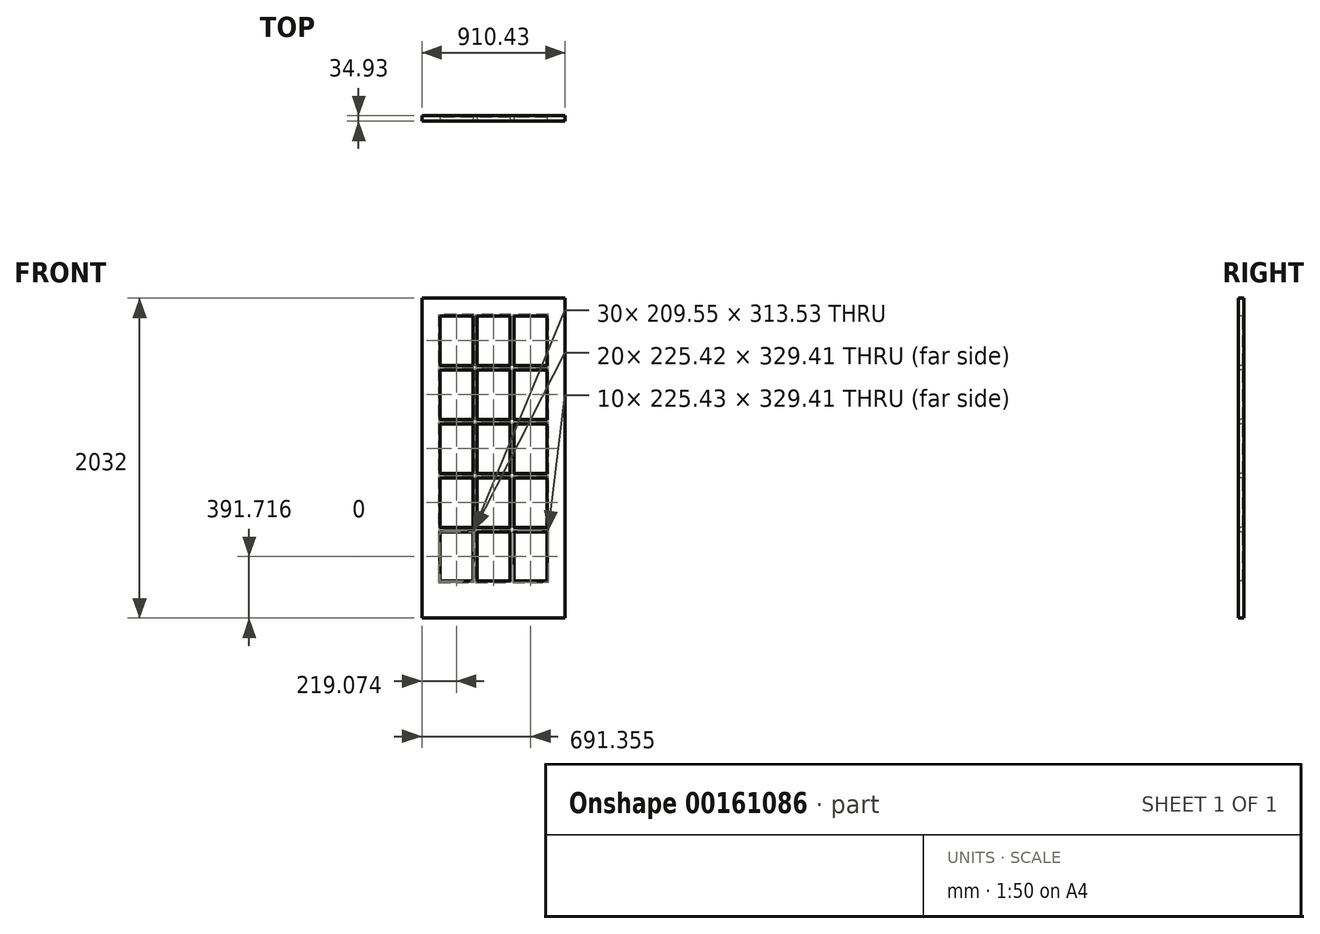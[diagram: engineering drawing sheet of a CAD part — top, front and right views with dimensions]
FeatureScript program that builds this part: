
annotation { "Feature Type Name" : "Feature", "Feature Type Description" : "" }
export const myFeature = defineFeature(function(context is Context, id is Id, definition is map)
    precondition{}
    {
        {
            var Q0;
            Q0=qCreatedBy(makeId("Top.planeOp"),FACE);
            var sketch = newSketch(context, id + "F0", { "sketchPlane" : qUnion([Q0])});
            skLineSegment(sketch, "E0.bottom", {"start": v(0, 0) * mm, "end": v(-910.43, 0) * mm});
            skLineSegment(sketch, "E0.top", {"start": v(0, 34.93) * mm, "end": v(-910.43, 34.93) * mm});
            skLineSegment(sketch, "E0.left", {"start": v(0, 0) * mm, "end": v(0, 34.93) * mm});
            skLineSegment(sketch, "E0.right", {"start": v(-910.43, 0) * mm, "end": v(-910.43, 34.93) * mm});
            skSolve(sketch);
        }
        {
            var Q0;
            Q0=qSketchRegion(id+"F0",true);
            extrude(context, id + "F1", {"entities" : qUnion([Q0]), "depth" : 2032 * mm});
        }
        {
            var Q0;
            Q0=qCreatedBy(makeId("Front.planeOp"),FACE);
            var sketch = newSketch(context, id + "F2", { "sketchPlane" : qUnion([Q0])});
            skPoint(sketch, "E1.0", {"position": v(-910.43, 2032) * mm});
            skPoint(sketch, "E2.0", {"position": v(0, 2032) * mm});
            skPoint(sketch, "E3.0", {"position": v(-910.43, 0) * mm});
            skPoint(sketch, "E4.0", {"position": v(0, 0) * mm});
            skPoint(sketch, "E5.0", {"position": v(-910.43, 1016) * mm});
            skPoint(sketch, "E6.0", {"position": v(-455.22, 2032) * mm});
            skPoint(sketch, "E7.0", {"position": v(0, 1016) * mm});
            skPoint(sketch, "E8.0", {"position": v(-455.22, 0) * mm});
            skLineSegment(sketch, "E9", {"start": v(-910.43, -186.31) * mm, "end": v(-804.07, -186.31) * mm, "construction": true});
            skLineSegment(sketch, "E10", {"start": v(-804.07, -186.31) * mm, "end": v(-796.13, -186.31) * mm, "construction": true});
            skLineSegment(sketch, "E11", {"start": v(-796.13, -186.31) * mm, "end": v(-586.58, -186.31) * mm, "construction": true});
            skLineSegment(sketch, "E12", {"start": v(-586.58, -186.31) * mm, "end": v(-560, -186.31) * mm, "construction": true});
            skLineSegment(sketch, "E13", {"start": v(-560, -186.31) * mm, "end": v(-350.44, -186.31) * mm, "construction": true});
            skLineSegment(sketch, "E14", {"start": v(-350.44, -186.31) * mm, "end": v(-323.85, -186.31) * mm, "construction": true});
            skLineSegment(sketch, "E15", {"start": v(-323.85, -186.31) * mm, "end": v(-114.3, -186.31) * mm, "construction": true});
            skLineSegment(sketch, "E16", {"start": v(-114.3, -186.31) * mm, "end": v(-106.36, -186.31) * mm, "construction": true});
            skLineSegment(sketch, "E17", {"start": v(-106.36, -186.31) * mm, "end": v(0, -186.31) * mm, "construction": true});
            skLineSegment(sketch, "E18", {"start": v(-1196.98, 2032) * mm, "end": v(-1196.98, 1927.22) * mm, "construction": true});
            skLineSegment(sketch, "E19", {"start": v(-1196.98, 1927.22) * mm, "end": v(-1196.98, 1919.29) * mm, "construction": true});
            skLineSegment(sketch, "E20", {"start": v(-1196.98, 1919.29) * mm, "end": v(-1196.98, 1605.76) * mm, "construction": true});
            skLineSegment(sketch, "E21", {"start": v(-1196.98, 1605.76) * mm, "end": v(-1196.98, 1576.59) * mm, "construction": true});
            skLineSegment(sketch, "E22", {"start": v(-1196.98, 1576.59) * mm, "end": v(-1196.98, 1263.05) * mm, "construction": true});
            skLineSegment(sketch, "E23", {"start": v(-1196.98, 1263.05) * mm, "end": v(-1196.98, 1233.88) * mm, "construction": true});
            skLineSegment(sketch, "E24", {"start": v(-1196.98, 1233.88) * mm, "end": v(-1196.98, 920.35) * mm, "construction": true});
            skLineSegment(sketch, "E25", {"start": v(-1196.98, 920.35) * mm, "end": v(-1196.98, 891.18) * mm, "construction": true});
            skLineSegment(sketch, "E26", {"start": v(-1196.98, 577.65) * mm, "end": v(-1196.98, 548.48) * mm, "construction": true});
            skLineSegment(sketch, "E27", {"start": v(-1196.98, 234.95) * mm, "end": v(-1196.98, 227.01) * mm, "construction": true});
            skLineSegment(sketch, "E28", {"start": v(-1196.98, 227.01) * mm, "end": v(-1196.98, 0) * mm, "construction": true});
            skLineSegment(sketch, "E29", {"start": v(-1196.98, 548.48) * mm, "end": v(-1196.98, 234.95) * mm, "construction": true});
            skLineSegment(sketch, "E30", {"start": v(-1196.98, 891.18) * mm, "end": v(-1196.98, 577.65) * mm, "construction": true});
            skLineSegment(sketch, "E31.bottom", {"start": v(-796.13, 234.95) * mm, "end": v(-586.58, 234.95) * mm});
            skLineSegment(sketch, "E31.top", {"start": v(-796.13, 548.48) * mm, "end": v(-586.58, 548.48) * mm});
            skLineSegment(sketch, "E31.left", {"start": v(-796.13, 234.95) * mm, "end": v(-796.13, 548.48) * mm});
            skLineSegment(sketch, "E31.right", {"start": v(-586.58, 234.95) * mm, "end": v(-586.58, 548.48) * mm});
            skLineSegment(sketch, "E32.bottom", {"start": v(-560, 234.95) * mm, "end": v(-350.44, 234.95) * mm});
            skLineSegment(sketch, "E32.top", {"start": v(-560, 548.48) * mm, "end": v(-350.44, 548.48) * mm});
            skLineSegment(sketch, "E32.left", {"start": v(-560, 234.95) * mm, "end": v(-560, 548.48) * mm});
            skLineSegment(sketch, "E32.right", {"start": v(-350.44, 234.95) * mm, "end": v(-350.44, 548.48) * mm});
            skLineSegment(sketch, "E33.bottom", {"start": v(-323.85, 548.48) * mm, "end": v(-114.3, 548.48) * mm});
            skLineSegment(sketch, "E33.top", {"start": v(-323.85, 234.95) * mm, "end": v(-114.3, 234.95) * mm});
            skLineSegment(sketch, "E33.left", {"start": v(-323.85, 548.48) * mm, "end": v(-323.85, 234.95) * mm});
            skLineSegment(sketch, "E33.right", {"start": v(-114.3, 548.48) * mm, "end": v(-114.3, 234.95) * mm});
            skLineSegment(sketch, "E34.bottom", {"start": v(-796.13, 577.65) * mm, "end": v(-586.58, 577.65) * mm});
            skLineSegment(sketch, "E34.top", {"start": v(-796.13, 891.18) * mm, "end": v(-586.58, 891.18) * mm});
            skLineSegment(sketch, "E34.left", {"start": v(-796.13, 577.65) * mm, "end": v(-796.13, 891.18) * mm});
            skLineSegment(sketch, "E34.right", {"start": v(-586.58, 577.65) * mm, "end": v(-586.58, 891.18) * mm});
            skLineSegment(sketch, "E35.bottom", {"start": v(-560, 577.65) * mm, "end": v(-350.44, 577.65) * mm});
            skLineSegment(sketch, "E35.top", {"start": v(-560, 891.18) * mm, "end": v(-350.44, 891.18) * mm});
            skLineSegment(sketch, "E35.left", {"start": v(-560, 577.65) * mm, "end": v(-560, 891.18) * mm});
            skLineSegment(sketch, "E35.right", {"start": v(-350.44, 577.65) * mm, "end": v(-350.44, 891.18) * mm});
            skLineSegment(sketch, "E36.bottom", {"start": v(-323.85, 577.65) * mm, "end": v(-114.3, 577.65) * mm});
            skLineSegment(sketch, "E36.top", {"start": v(-323.85, 891.18) * mm, "end": v(-114.3, 891.18) * mm});
            skLineSegment(sketch, "E36.left", {"start": v(-323.85, 577.65) * mm, "end": v(-323.85, 891.18) * mm});
            skLineSegment(sketch, "E36.right", {"start": v(-114.3, 577.65) * mm, "end": v(-114.3, 891.18) * mm});
            skLineSegment(sketch, "E37.bottom", {"start": v(-796.13, 920.35) * mm, "end": v(-586.58, 920.35) * mm});
            skLineSegment(sketch, "E37.top", {"start": v(-796.13, 1233.88) * mm, "end": v(-586.58, 1233.88) * mm});
            skLineSegment(sketch, "E37.left", {"start": v(-796.13, 920.35) * mm, "end": v(-796.13, 1233.88) * mm});
            skLineSegment(sketch, "E37.right", {"start": v(-586.58, 920.35) * mm, "end": v(-586.58, 1233.88) * mm});
            skLineSegment(sketch, "E38.bottom", {"start": v(-560, 920.35) * mm, "end": v(-350.44, 920.35) * mm});
            skLineSegment(sketch, "E38.top", {"start": v(-560, 1233.88) * mm, "end": v(-350.44, 1233.88) * mm});
            skLineSegment(sketch, "E38.left", {"start": v(-560, 920.35) * mm, "end": v(-560, 1233.88) * mm});
            skLineSegment(sketch, "E38.right", {"start": v(-350.44, 920.35) * mm, "end": v(-350.44, 1233.88) * mm});
            skLineSegment(sketch, "E39.bottom", {"start": v(-323.85, 920.35) * mm, "end": v(-114.3, 920.35) * mm});
            skLineSegment(sketch, "E39.top", {"start": v(-323.85, 1233.88) * mm, "end": v(-114.3, 1233.88) * mm});
            skLineSegment(sketch, "E39.left", {"start": v(-323.85, 920.35) * mm, "end": v(-323.85, 1233.88) * mm});
            skLineSegment(sketch, "E39.right", {"start": v(-114.3, 920.35) * mm, "end": v(-114.3, 1233.88) * mm});
            skLineSegment(sketch, "E40.bottom", {"start": v(-796.13, 1263.05) * mm, "end": v(-586.58, 1263.05) * mm});
            skLineSegment(sketch, "E40.top", {"start": v(-796.13, 1576.59) * mm, "end": v(-586.58, 1576.59) * mm});
            skLineSegment(sketch, "E40.left", {"start": v(-796.13, 1263.05) * mm, "end": v(-796.13, 1576.59) * mm});
            skLineSegment(sketch, "E40.right", {"start": v(-586.58, 1263.05) * mm, "end": v(-586.58, 1576.59) * mm});
            skLineSegment(sketch, "E41.bottom", {"start": v(-560, 1263.05) * mm, "end": v(-350.44, 1263.05) * mm});
            skLineSegment(sketch, "E41.top", {"start": v(-560, 1576.59) * mm, "end": v(-350.44, 1576.59) * mm});
            skLineSegment(sketch, "E41.left", {"start": v(-560, 1263.05) * mm, "end": v(-560, 1576.59) * mm});
            skLineSegment(sketch, "E41.right", {"start": v(-350.44, 1263.05) * mm, "end": v(-350.44, 1576.59) * mm});
            skLineSegment(sketch, "E42.bottom", {"start": v(-323.85, 1263.05) * mm, "end": v(-114.3, 1263.05) * mm});
            skLineSegment(sketch, "E42.top", {"start": v(-323.85, 1576.59) * mm, "end": v(-114.3, 1576.59) * mm});
            skLineSegment(sketch, "E42.left", {"start": v(-323.85, 1263.05) * mm, "end": v(-323.85, 1576.59) * mm});
            skLineSegment(sketch, "E42.right", {"start": v(-114.3, 1263.05) * mm, "end": v(-114.3, 1576.59) * mm});
            skLineSegment(sketch, "E43.bottom", {"start": v(-796.13, 1605.76) * mm, "end": v(-586.58, 1605.76) * mm});
            skLineSegment(sketch, "E43.top", {"start": v(-796.13, 1919.29) * mm, "end": v(-586.58, 1919.29) * mm});
            skLineSegment(sketch, "E43.left", {"start": v(-796.13, 1605.76) * mm, "end": v(-796.13, 1919.29) * mm});
            skLineSegment(sketch, "E43.right", {"start": v(-586.58, 1605.76) * mm, "end": v(-586.58, 1919.29) * mm});
            skLineSegment(sketch, "E44.bottom", {"start": v(-560, 1605.76) * mm, "end": v(-350.44, 1605.76) * mm});
            skLineSegment(sketch, "E44.top", {"start": v(-560, 1919.29) * mm, "end": v(-350.44, 1919.29) * mm});
            skLineSegment(sketch, "E44.left", {"start": v(-560, 1605.76) * mm, "end": v(-560, 1919.29) * mm});
            skLineSegment(sketch, "E44.right", {"start": v(-350.44, 1605.76) * mm, "end": v(-350.44, 1919.29) * mm});
            skLineSegment(sketch, "E45.bottom", {"start": v(-323.85, 1605.76) * mm, "end": v(-114.3, 1605.76) * mm});
            skLineSegment(sketch, "E45.top", {"start": v(-323.85, 1919.29) * mm, "end": v(-114.3, 1919.29) * mm});
            skLineSegment(sketch, "E45.left", {"start": v(-323.85, 1605.76) * mm, "end": v(-323.85, 1919.29) * mm});
            skLineSegment(sketch, "E45.right", {"start": v(-114.3, 1605.76) * mm, "end": v(-114.3, 1919.29) * mm});
            skSolve(sketch);
        }
        {
            var Q0;
            Q0 = qSketchRegion(id + "F2", true);
            extrude(context, id + "F3", {"entities" : qUnion([Q0]), "operationType" : NewBodyOperationType.REMOVE, "endBound" : BoundingType.THROUGH_ALL, "oppositeDirection" : true, "depth" : 426.72 * mm});
        }
        {
            var Q0;
            Q0=makeQuery(id+"F3.boolean.opBoolean","COPY",EDGE,{"derivedFrom":makeQuery(id+"F3.opExtrude","CAP_EDGE",EDGE,{"disambiguationData":[OSD([sQuery(id+"F2.wireOp",EDGE,"E43.right")])],"isStart":true})});
            var Q1;
            Q1=makeQuery(id+"F3.boolean.opBoolean","COPY",EDGE,{"derivedFrom":makeQuery(id+"F3.opExtrude","CAP_EDGE",EDGE,{"disambiguationData":[OSD([sQuery(id+"F2.wireOp",EDGE,"E43.bottom")])],"isStart":true})});
            var Q2;
            Q2=makeQuery(id+"F3.boolean.opBoolean","COPY",EDGE,{"derivedFrom":makeQuery(id+"F3.opExtrude","CAP_EDGE",EDGE,{"disambiguationData":[OSD([sQuery(id+"F2.wireOp",EDGE,"E44.left")])],"isStart":true})});
            var Q3;
            Q3=makeQuery(id+"F3.boolean.opBoolean","COPY",EDGE,{"derivedFrom":makeQuery(id+"F3.opExtrude","CAP_EDGE",EDGE,{"disambiguationData":[OSD([sQuery(id+"F2.wireOp",EDGE,"E44.bottom")])],"isStart":true})});
            var Q4;
            Q4=makeQuery(id+"F3.boolean.opBoolean","COPY",EDGE,{"derivedFrom":makeQuery(id+"F3.opExtrude","CAP_EDGE",EDGE,{"disambiguationData":[OSD([sQuery(id+"F2.wireOp",EDGE,"E41.left")])],"isStart":true})});
            var Q5;
            Q5=makeQuery(id+"F3.boolean.opBoolean","COPY",EDGE,{"derivedFrom":makeQuery(id+"F3.opExtrude","CAP_EDGE",EDGE,{"disambiguationData":[OSD([sQuery(id+"F2.wireOp",EDGE,"E40.top")])],"isStart":true})});
            var Q6;
            Q6=makeQuery(id+"F3.boolean.opBoolean","COPY",EDGE,{"derivedFrom":makeQuery(id+"F3.opExtrude","CAP_EDGE",EDGE,{"disambiguationData":[OSD([sQuery(id+"F2.wireOp",EDGE,"E40.right")])],"isStart":true})});
            var Q7;
            Q7=makeQuery(id+"F3.boolean.opBoolean","COPY",EDGE,{"derivedFrom":makeQuery(id+"F3.opExtrude","CAP_EDGE",EDGE,{"disambiguationData":[OSD([sQuery(id+"F2.wireOp",EDGE,"E44.right")])],"isStart":true})});
            var Q8;
            Q8=makeQuery(id+"F3.boolean.opBoolean","COPY",EDGE,{"derivedFrom":makeQuery(id+"F3.opExtrude","CAP_EDGE",EDGE,{"disambiguationData":[OSD([sQuery(id+"F2.wireOp",EDGE,"E41.top")])],"isStart":true})});
            var Q9;
            Q9=makeQuery(id+"F3.boolean.opBoolean","COPY",EDGE,{"derivedFrom":makeQuery(id+"F3.opExtrude","CAP_EDGE",EDGE,{"disambiguationData":[OSD([sQuery(id+"F2.wireOp",EDGE,"E41.right")])],"isStart":true})});
            var Q10;
            Q10=makeQuery(id+"F3.boolean.opBoolean","COPY",EDGE,{"derivedFrom":makeQuery(id+"F3.opExtrude","CAP_EDGE",EDGE,{"disambiguationData":[OSD([sQuery(id+"F2.wireOp",EDGE,"E42.left")])],"isStart":true})});
            var Q11;
            Q11=makeQuery(id+"F3.boolean.opBoolean","COPY",EDGE,{"derivedFrom":makeQuery(id+"F3.opExtrude","CAP_EDGE",EDGE,{"disambiguationData":[OSD([sQuery(id+"F2.wireOp",EDGE,"E42.top")])],"isStart":true})});
            var Q12;
            Q12=makeQuery(id+"F3.boolean.opBoolean","COPY",EDGE,{"derivedFrom":makeQuery(id+"F3.opExtrude","CAP_EDGE",EDGE,{"disambiguationData":[OSD([sQuery(id+"F2.wireOp",EDGE,"E45.bottom")])],"isStart":true})});
            var Q13;
            Q13=makeQuery(id+"F3.boolean.opBoolean","COPY",EDGE,{"derivedFrom":makeQuery(id+"F3.opExtrude","CAP_EDGE",EDGE,{"disambiguationData":[OSD([sQuery(id+"F2.wireOp",EDGE,"E45.left")])],"isStart":true})});
            var Q14;
            Q14=makeQuery(id+"F3.boolean.opBoolean","COPY",EDGE,{"derivedFrom":makeQuery(id+"F3.opExtrude","CAP_EDGE",EDGE,{"disambiguationData":[OSD([sQuery(id+"F2.wireOp",EDGE,"E40.bottom")])],"isStart":true})});
            var Q15;
            Q15=makeQuery(id+"F3.boolean.opBoolean","COPY",EDGE,{"derivedFrom":makeQuery(id+"F3.opExtrude","CAP_EDGE",EDGE,{"disambiguationData":[OSD([sQuery(id+"F2.wireOp",EDGE,"E37.top")])],"isStart":true})});
            var Q16;
            Q16=makeQuery(id+"F3.boolean.opBoolean","COPY",EDGE,{"derivedFrom":makeQuery(id+"F3.opExtrude","CAP_EDGE",EDGE,{"disambiguationData":[OSD([sQuery(id+"F2.wireOp",EDGE,"E37.bottom")])],"isStart":true})});
            var Q17;
            Q17=makeQuery(id+"F3.boolean.opBoolean","COPY",EDGE,{"derivedFrom":makeQuery(id+"F3.opExtrude","CAP_EDGE",EDGE,{"disambiguationData":[OSD([sQuery(id+"F2.wireOp",EDGE,"E34.top")])],"isStart":true})});
            var Q18;
            Q18=makeQuery(id+"F3.boolean.opBoolean","COPY",EDGE,{"derivedFrom":makeQuery(id+"F3.opExtrude","CAP_EDGE",EDGE,{"disambiguationData":[OSD([sQuery(id+"F2.wireOp",EDGE,"E34.bottom")])],"isStart":true})});
            var Q19;
            Q19=makeQuery(id+"F3.boolean.opBoolean","COPY",EDGE,{"derivedFrom":makeQuery(id+"F3.opExtrude","CAP_EDGE",EDGE,{"disambiguationData":[OSD([sQuery(id+"F2.wireOp",EDGE,"E31.top")])],"isStart":true})});
            var Q20;
            Q20=makeQuery(id+"F3.boolean.opBoolean","COPY",EDGE,{"derivedFrom":makeQuery(id+"F3.opExtrude","CAP_EDGE",EDGE,{"disambiguationData":[OSD([sQuery(id+"F2.wireOp",EDGE,"E31.bottom")])],"isStart":true})});
            var Q21;
            Q21=makeQuery(id+"F3.boolean.opBoolean","COPY",EDGE,{"derivedFrom":makeQuery(id+"F3.opExtrude","CAP_EDGE",EDGE,{"disambiguationData":[OSD([sQuery(id+"F2.wireOp",EDGE,"E43.top")])],"isStart":true})});
            var Q22;
            Q22=makeQuery(id+"F3.boolean.opBoolean","COPY",EDGE,{"derivedFrom":makeQuery(id+"F3.opExtrude","CAP_EDGE",EDGE,{"disambiguationData":[OSD([sQuery(id+"F2.wireOp",EDGE,"E43.left")])],"isStart":true})});
            var Q23;
            Q23=makeQuery(id+"F3.boolean.opBoolean","COPY",EDGE,{"derivedFrom":makeQuery(id+"F3.opExtrude","CAP_EDGE",EDGE,{"disambiguationData":[OSD([sQuery(id+"F2.wireOp",EDGE,"E40.left")])],"isStart":true})});
            var Q24;
            Q24=makeQuery(id+"F3.boolean.opBoolean","COPY",EDGE,{"derivedFrom":makeQuery(id+"F3.opExtrude","CAP_EDGE",EDGE,{"disambiguationData":[OSD([sQuery(id+"F2.wireOp",EDGE,"E37.left")])],"isStart":true})});
            var Q25;
            Q25=makeQuery(id+"F3.boolean.opBoolean","COPY",EDGE,{"derivedFrom":makeQuery(id+"F3.opExtrude","CAP_EDGE",EDGE,{"disambiguationData":[OSD([sQuery(id+"F2.wireOp",EDGE,"E34.left")])],"isStart":true})});
            var Q26;
            Q26=makeQuery(id+"F3.boolean.opBoolean","COPY",EDGE,{"derivedFrom":makeQuery(id+"F3.opExtrude","CAP_EDGE",EDGE,{"disambiguationData":[OSD([sQuery(id+"F2.wireOp",EDGE,"E31.left")])],"isStart":true})});
            var Q27;
            Q27=makeQuery(id+"F3.boolean.opBoolean","COPY",EDGE,{"derivedFrom":makeQuery(id+"F3.opExtrude","CAP_EDGE",EDGE,{"disambiguationData":[OSD([sQuery(id+"F2.wireOp",EDGE,"E31.right")])],"isStart":true})});
            var Q28;
            Q28=makeQuery(id+"F3.boolean.opBoolean","COPY",EDGE,{"derivedFrom":makeQuery(id+"F3.opExtrude","CAP_EDGE",EDGE,{"disambiguationData":[OSD([sQuery(id+"F2.wireOp",EDGE,"E34.right")])],"isStart":true})});
            var Q29;
            Q29=makeQuery(id+"F3.boolean.opBoolean","COPY",EDGE,{"derivedFrom":makeQuery(id+"F3.opExtrude","CAP_EDGE",EDGE,{"disambiguationData":[OSD([sQuery(id+"F2.wireOp",EDGE,"E37.right")])],"isStart":true})});
            var Q30;
            Q30=makeQuery(id+"F3.boolean.opBoolean","COPY",EDGE,{"derivedFrom":makeQuery(id+"F3.opExtrude","CAP_EDGE",EDGE,{"disambiguationData":[OSD([sQuery(id+"F2.wireOp",EDGE,"E44.top")])],"isStart":true})});
            var Q31;
            Q31=makeQuery(id+"F3.boolean.opBoolean","COPY",EDGE,{"derivedFrom":makeQuery(id+"F3.opExtrude","CAP_EDGE",EDGE,{"disambiguationData":[OSD([sQuery(id+"F2.wireOp",EDGE,"E45.top")])],"isStart":true})});
            var Q32;
            Q32=makeQuery(id+"F3.boolean.opBoolean","COPY",EDGE,{"derivedFrom":makeQuery(id+"F3.opExtrude","CAP_EDGE",EDGE,{"disambiguationData":[OSD([sQuery(id+"F2.wireOp",EDGE,"E45.right")])],"isStart":true})});
            var Q33;
            Q33=makeQuery(id+"F3.boolean.opBoolean","COPY",EDGE,{"derivedFrom":makeQuery(id+"F3.opExtrude","CAP_EDGE",EDGE,{"disambiguationData":[OSD([sQuery(id+"F2.wireOp",EDGE,"E42.right")])],"isStart":true})});
            var Q34;
            Q34=makeQuery(id+"F3.boolean.opBoolean","COPY",EDGE,{"derivedFrom":makeQuery(id+"F3.opExtrude","CAP_EDGE",EDGE,{"disambiguationData":[OSD([sQuery(id+"F2.wireOp",EDGE,"E39.right")])],"isStart":true})});
            var Q35;
            Q35=makeQuery(id+"F3.boolean.opBoolean","COPY",EDGE,{"derivedFrom":makeQuery(id+"F3.opExtrude","CAP_EDGE",EDGE,{"disambiguationData":[OSD([sQuery(id+"F2.wireOp",EDGE,"E36.right")])],"isStart":true})});
            var Q36;
            Q36=makeQuery(id+"F3.boolean.opBoolean","COPY",EDGE,{"derivedFrom":makeQuery(id+"F3.opExtrude","CAP_EDGE",EDGE,{"disambiguationData":[OSD([sQuery(id+"F2.wireOp",EDGE,"E33.right")])],"isStart":true})});
            var Q37;
            Q37=makeQuery(id+"F3.boolean.opBoolean","COPY",EDGE,{"derivedFrom":makeQuery(id+"F3.opExtrude","CAP_EDGE",EDGE,{"disambiguationData":[OSD([sQuery(id+"F2.wireOp",EDGE,"E33.top")])],"isStart":true})});
            var Q38;
            Q38=makeQuery(id+"F3.boolean.opBoolean","COPY",EDGE,{"derivedFrom":makeQuery(id+"F3.opExtrude","CAP_EDGE",EDGE,{"disambiguationData":[OSD([sQuery(id+"F2.wireOp",EDGE,"E32.bottom")])],"isStart":true})});
            var Q39;
            Q39=makeQuery(id+"F3.boolean.opBoolean","COPY",EDGE,{"derivedFrom":makeQuery(id+"F3.opExtrude","CAP_EDGE",EDGE,{"disambiguationData":[OSD([sQuery(id+"F2.wireOp",EDGE,"E32.left")])],"isStart":true})});
            var Q40;
            Q40=makeQuery(id+"F3.boolean.opBoolean","COPY",EDGE,{"derivedFrom":makeQuery(id+"F3.opExtrude","CAP_EDGE",EDGE,{"disambiguationData":[OSD([sQuery(id+"F2.wireOp",EDGE,"E35.left")])],"isStart":true})});
            var Q41;
            Q41=makeQuery(id+"F3.boolean.opBoolean","COPY",EDGE,{"derivedFrom":makeQuery(id+"F3.opExtrude","CAP_EDGE",EDGE,{"disambiguationData":[OSD([sQuery(id+"F2.wireOp",EDGE,"E38.left")])],"isStart":true})});
            var Q42;
            Q42=makeQuery(id+"F3.boolean.opBoolean","COPY",EDGE,{"derivedFrom":makeQuery(id+"F3.opExtrude","CAP_EDGE",EDGE,{"disambiguationData":[OSD([sQuery(id+"F2.wireOp",EDGE,"E33.left")])],"isStart":true})});
            var Q43;
            Q43=makeQuery(id+"F3.boolean.opBoolean","COPY",EDGE,{"derivedFrom":makeQuery(id+"F3.opExtrude","CAP_EDGE",EDGE,{"disambiguationData":[OSD([sQuery(id+"F2.wireOp",EDGE,"E32.right")])],"isStart":true})});
            var Q44;
            Q44=makeQuery(id+"F3.boolean.opBoolean","COPY",EDGE,{"derivedFrom":makeQuery(id+"F3.opExtrude","CAP_EDGE",EDGE,{"disambiguationData":[OSD([sQuery(id+"F2.wireOp",EDGE,"E32.top")])],"isStart":true})});
            var Q45;
            Q45=makeQuery(id+"F3.boolean.opBoolean","COPY",EDGE,{"derivedFrom":makeQuery(id+"F3.opExtrude","CAP_EDGE",EDGE,{"disambiguationData":[OSD([sQuery(id+"F2.wireOp",EDGE,"E33.bottom")])],"isStart":true})});
            var Q46;
            Q46=makeQuery(id+"F3.boolean.opBoolean","COPY",EDGE,{"derivedFrom":makeQuery(id+"F3.opExtrude","CAP_EDGE",EDGE,{"disambiguationData":[OSD([sQuery(id+"F2.wireOp",EDGE,"E36.bottom")])],"isStart":true})});
            var Q47;
            Q47=makeQuery(id+"F3.boolean.opBoolean","COPY",EDGE,{"derivedFrom":makeQuery(id+"F3.opExtrude","CAP_EDGE",EDGE,{"disambiguationData":[OSD([sQuery(id+"F2.wireOp",EDGE,"E35.bottom")])],"isStart":true})});
            var Q48;
            Q48=makeQuery(id+"F3.boolean.opBoolean","COPY",EDGE,{"derivedFrom":makeQuery(id+"F3.opExtrude","CAP_EDGE",EDGE,{"disambiguationData":[OSD([sQuery(id+"F2.wireOp",EDGE,"E35.right")])],"isStart":true})});
            var Q49;
            Q49=makeQuery(id+"F3.boolean.opBoolean","COPY",EDGE,{"derivedFrom":makeQuery(id+"F3.opExtrude","CAP_EDGE",EDGE,{"disambiguationData":[OSD([sQuery(id+"F2.wireOp",EDGE,"E36.left")])],"isStart":true})});
            var Q50;
            Q50=makeQuery(id+"F3.boolean.opBoolean","COPY",EDGE,{"derivedFrom":makeQuery(id+"F3.opExtrude","CAP_EDGE",EDGE,{"disambiguationData":[OSD([sQuery(id+"F2.wireOp",EDGE,"E36.top")])],"isStart":true})});
            var Q51;
            Q51=makeQuery(id+"F3.boolean.opBoolean","COPY",EDGE,{"derivedFrom":makeQuery(id+"F3.opExtrude","CAP_EDGE",EDGE,{"disambiguationData":[OSD([sQuery(id+"F2.wireOp",EDGE,"E35.top")])],"isStart":true})});
            var Q52;
            Q52=makeQuery(id+"F3.boolean.opBoolean","COPY",EDGE,{"derivedFrom":makeQuery(id+"F3.opExtrude","CAP_EDGE",EDGE,{"disambiguationData":[OSD([sQuery(id+"F2.wireOp",EDGE,"E38.bottom")])],"isStart":true})});
            var Q53;
            Q53=makeQuery(id+"F3.boolean.opBoolean","COPY",EDGE,{"derivedFrom":makeQuery(id+"F3.opExtrude","CAP_EDGE",EDGE,{"disambiguationData":[OSD([sQuery(id+"F2.wireOp",EDGE,"E39.bottom")])],"isStart":true})});
            var Q54;
            Q54=makeQuery(id+"F3.boolean.opBoolean","COPY",EDGE,{"derivedFrom":makeQuery(id+"F3.opExtrude","CAP_EDGE",EDGE,{"disambiguationData":[OSD([sQuery(id+"F2.wireOp",EDGE,"E39.left")])],"isStart":true})});
            var Q55;
            Q55=makeQuery(id+"F3.boolean.opBoolean","COPY",EDGE,{"derivedFrom":makeQuery(id+"F3.opExtrude","CAP_EDGE",EDGE,{"disambiguationData":[OSD([sQuery(id+"F2.wireOp",EDGE,"E38.right")])],"isStart":true})});
            var Q56;
            Q56=makeQuery(id+"F3.boolean.opBoolean","COPY",EDGE,{"derivedFrom":makeQuery(id+"F3.opExtrude","CAP_EDGE",EDGE,{"disambiguationData":[OSD([sQuery(id+"F2.wireOp",EDGE,"E38.top")])],"isStart":true})});
            var Q57;
            Q57=makeQuery(id+"F3.boolean.opBoolean","COPY",EDGE,{"derivedFrom":makeQuery(id+"F3.opExtrude","CAP_EDGE",EDGE,{"disambiguationData":[OSD([sQuery(id+"F2.wireOp",EDGE,"E41.bottom")])],"isStart":true})});
            var Q58;
            Q58=makeQuery(id+"F3.boolean.opBoolean","COPY",EDGE,{"derivedFrom":makeQuery(id+"F3.opExtrude","CAP_EDGE",EDGE,{"disambiguationData":[OSD([sQuery(id+"F2.wireOp",EDGE,"E42.bottom")])],"isStart":true})});
            var Q59;
            Q59=makeQuery(id+"F3.boolean.opBoolean","COPY",EDGE,{"derivedFrom":makeQuery(id+"F3.opExtrude","CAP_EDGE",EDGE,{"disambiguationData":[OSD([sQuery(id+"F2.wireOp",EDGE,"E39.top")])],"isStart":true})});
            var Q60;
            Q60=makeQuery(id+"F3.boolean.opBoolean","INTERSECT",EDGE,{"derivedFrom":[makeQuery(id+"F1.opExtrude","SWEPT_FACE",FACE,{"disambiguationData":[OSD([sQuery(id+"F0.wireOp",EDGE,"E0.top")])]}),makeQuery(id+"F3.opExtrude","SWEPT_FACE",FACE,{"disambiguationData":[OSD([sQuery(id+"F2.wireOp",EDGE,"E31.bottom")])]})]});
            var Q61;
            Q61=makeQuery(id+"F3.boolean.opBoolean","INTERSECT",EDGE,{"derivedFrom":[makeQuery(id+"F1.opExtrude","SWEPT_FACE",FACE,{"disambiguationData":[OSD([sQuery(id+"F0.wireOp",EDGE,"E0.top")])]}),makeQuery(id+"F3.opExtrude","SWEPT_FACE",FACE,{"disambiguationData":[OSD([sQuery(id+"F2.wireOp",EDGE,"E32.bottom")])]})]});
            var Q62;
            Q62=makeQuery(id+"F3.boolean.opBoolean","INTERSECT",EDGE,{"derivedFrom":[makeQuery(id+"F1.opExtrude","SWEPT_FACE",FACE,{"disambiguationData":[OSD([sQuery(id+"F0.wireOp",EDGE,"E0.top")])]}),makeQuery(id+"F3.opExtrude","SWEPT_FACE",FACE,{"disambiguationData":[OSD([sQuery(id+"F2.wireOp",EDGE,"E33.top")])]})]});
            var Q63;
            Q63=makeQuery(id+"F3.boolean.opBoolean","INTERSECT",EDGE,{"derivedFrom":[makeQuery(id+"F1.opExtrude","SWEPT_FACE",FACE,{"disambiguationData":[OSD([sQuery(id+"F0.wireOp",EDGE,"E0.top")])]}),makeQuery(id+"F3.opExtrude","SWEPT_FACE",FACE,{"disambiguationData":[OSD([sQuery(id+"F2.wireOp",EDGE,"E33.right")])]})]});
            var Q64;
            Q64=makeQuery(id+"F3.boolean.opBoolean","INTERSECT",EDGE,{"derivedFrom":[makeQuery(id+"F1.opExtrude","SWEPT_FACE",FACE,{"disambiguationData":[OSD([sQuery(id+"F0.wireOp",EDGE,"E0.top")])]}),makeQuery(id+"F3.opExtrude","SWEPT_FACE",FACE,{"disambiguationData":[OSD([sQuery(id+"F2.wireOp",EDGE,"E36.right")])]})]});
            var Q65;
            Q65=makeQuery(id+"F3.boolean.opBoolean","INTERSECT",EDGE,{"derivedFrom":[makeQuery(id+"F1.opExtrude","SWEPT_FACE",FACE,{"disambiguationData":[OSD([sQuery(id+"F0.wireOp",EDGE,"E0.top")])]}),makeQuery(id+"F3.opExtrude","SWEPT_FACE",FACE,{"disambiguationData":[OSD([sQuery(id+"F2.wireOp",EDGE,"E39.right")])]})]});
            var Q66;
            Q66=makeQuery(id+"F3.boolean.opBoolean","INTERSECT",EDGE,{"derivedFrom":[makeQuery(id+"F1.opExtrude","SWEPT_FACE",FACE,{"disambiguationData":[OSD([sQuery(id+"F0.wireOp",EDGE,"E0.top")])]}),makeQuery(id+"F3.opExtrude","SWEPT_FACE",FACE,{"disambiguationData":[OSD([sQuery(id+"F2.wireOp",EDGE,"E42.right")])]})]});
            var Q67;
            Q67=makeQuery(id+"F3.boolean.opBoolean","INTERSECT",EDGE,{"derivedFrom":[makeQuery(id+"F1.opExtrude","SWEPT_FACE",FACE,{"disambiguationData":[OSD([sQuery(id+"F0.wireOp",EDGE,"E0.top")])]}),makeQuery(id+"F3.opExtrude","SWEPT_FACE",FACE,{"disambiguationData":[OSD([sQuery(id+"F2.wireOp",EDGE,"E45.right")])]})]});
            var Q68;
            Q68=makeQuery(id+"F3.boolean.opBoolean","INTERSECT",EDGE,{"derivedFrom":[makeQuery(id+"F1.opExtrude","SWEPT_FACE",FACE,{"disambiguationData":[OSD([sQuery(id+"F0.wireOp",EDGE,"E0.top")])]}),makeQuery(id+"F3.opExtrude","SWEPT_FACE",FACE,{"disambiguationData":[OSD([sQuery(id+"F2.wireOp",EDGE,"E45.top")])]})]});
            var Q69;
            Q69=makeQuery(id+"F3.boolean.opBoolean","INTERSECT",EDGE,{"derivedFrom":[makeQuery(id+"F1.opExtrude","SWEPT_FACE",FACE,{"disambiguationData":[OSD([sQuery(id+"F0.wireOp",EDGE,"E0.top")])]}),makeQuery(id+"F3.opExtrude","SWEPT_FACE",FACE,{"disambiguationData":[OSD([sQuery(id+"F2.wireOp",EDGE,"E44.top")])]})]});
            var Q70;
            Q70=makeQuery(id+"F3.boolean.opBoolean","INTERSECT",EDGE,{"derivedFrom":[makeQuery(id+"F1.opExtrude","SWEPT_FACE",FACE,{"disambiguationData":[OSD([sQuery(id+"F0.wireOp",EDGE,"E0.top")])]}),makeQuery(id+"F3.opExtrude","SWEPT_FACE",FACE,{"disambiguationData":[OSD([sQuery(id+"F2.wireOp",EDGE,"E43.top")])]})]});
            var Q71;
            Q71=makeQuery(id+"F3.boolean.opBoolean","INTERSECT",EDGE,{"derivedFrom":[makeQuery(id+"F1.opExtrude","SWEPT_FACE",FACE,{"disambiguationData":[OSD([sQuery(id+"F0.wireOp",EDGE,"E0.top")])]}),makeQuery(id+"F3.opExtrude","SWEPT_FACE",FACE,{"disambiguationData":[OSD([sQuery(id+"F2.wireOp",EDGE,"E43.left")])]})]});
            var Q72;
            Q72=makeQuery(id+"F3.boolean.opBoolean","INTERSECT",EDGE,{"derivedFrom":[makeQuery(id+"F1.opExtrude","SWEPT_FACE",FACE,{"disambiguationData":[OSD([sQuery(id+"F0.wireOp",EDGE,"E0.top")])]}),makeQuery(id+"F3.opExtrude","SWEPT_FACE",FACE,{"disambiguationData":[OSD([sQuery(id+"F2.wireOp",EDGE,"E40.left")])]})]});
            var Q73;
            Q73=makeQuery(id+"F3.boolean.opBoolean","INTERSECT",EDGE,{"derivedFrom":[makeQuery(id+"F1.opExtrude","SWEPT_FACE",FACE,{"disambiguationData":[OSD([sQuery(id+"F0.wireOp",EDGE,"E0.top")])]}),makeQuery(id+"F3.opExtrude","SWEPT_FACE",FACE,{"disambiguationData":[OSD([sQuery(id+"F2.wireOp",EDGE,"E37.left")])]})]});
            var Q74;
            Q74=makeQuery(id+"F3.boolean.opBoolean","INTERSECT",EDGE,{"derivedFrom":[makeQuery(id+"F1.opExtrude","SWEPT_FACE",FACE,{"disambiguationData":[OSD([sQuery(id+"F0.wireOp",EDGE,"E0.top")])]}),makeQuery(id+"F3.opExtrude","SWEPT_FACE",FACE,{"disambiguationData":[OSD([sQuery(id+"F2.wireOp",EDGE,"E34.left")])]})]});
            var Q75;
            Q75=makeQuery(id+"F3.boolean.opBoolean","INTERSECT",EDGE,{"derivedFrom":[makeQuery(id+"F1.opExtrude","SWEPT_FACE",FACE,{"disambiguationData":[OSD([sQuery(id+"F0.wireOp",EDGE,"E0.top")])]}),makeQuery(id+"F3.opExtrude","SWEPT_FACE",FACE,{"disambiguationData":[OSD([sQuery(id+"F2.wireOp",EDGE,"E31.left")])]})]});
            var Q76;
            Q76=makeQuery(id+"F3.boolean.opBoolean","INTERSECT",EDGE,{"derivedFrom":[makeQuery(id+"F1.opExtrude","SWEPT_FACE",FACE,{"disambiguationData":[OSD([sQuery(id+"F0.wireOp",EDGE,"E0.top")])]}),makeQuery(id+"F3.opExtrude","SWEPT_FACE",FACE,{"disambiguationData":[OSD([sQuery(id+"F2.wireOp",EDGE,"E31.right")])]})]});
            var Q77;
            Q77=makeQuery(id+"F3.boolean.opBoolean","INTERSECT",EDGE,{"derivedFrom":[makeQuery(id+"F1.opExtrude","SWEPT_FACE",FACE,{"disambiguationData":[OSD([sQuery(id+"F0.wireOp",EDGE,"E0.top")])]}),makeQuery(id+"F3.opExtrude","SWEPT_FACE",FACE,{"disambiguationData":[OSD([sQuery(id+"F2.wireOp",EDGE,"E32.left")])]})]});
            var Q78;
            Q78=makeQuery(id+"F3.boolean.opBoolean","INTERSECT",EDGE,{"derivedFrom":[makeQuery(id+"F1.opExtrude","SWEPT_FACE",FACE,{"disambiguationData":[OSD([sQuery(id+"F0.wireOp",EDGE,"E0.top")])]}),makeQuery(id+"F3.opExtrude","SWEPT_FACE",FACE,{"disambiguationData":[OSD([sQuery(id+"F2.wireOp",EDGE,"E32.right")])]})]});
            var Q79;
            Q79=makeQuery(id+"F3.boolean.opBoolean","INTERSECT",EDGE,{"derivedFrom":[makeQuery(id+"F1.opExtrude","SWEPT_FACE",FACE,{"disambiguationData":[OSD([sQuery(id+"F0.wireOp",EDGE,"E0.top")])]}),makeQuery(id+"F3.opExtrude","SWEPT_FACE",FACE,{"disambiguationData":[OSD([sQuery(id+"F2.wireOp",EDGE,"E33.left")])]})]});
            var Q80;
            Q80=makeQuery(id+"F3.boolean.opBoolean","INTERSECT",EDGE,{"derivedFrom":[makeQuery(id+"F1.opExtrude","SWEPT_FACE",FACE,{"disambiguationData":[OSD([sQuery(id+"F0.wireOp",EDGE,"E0.top")])]}),makeQuery(id+"F3.opExtrude","SWEPT_FACE",FACE,{"disambiguationData":[OSD([sQuery(id+"F2.wireOp",EDGE,"E33.bottom")])]})]});
            var Q81;
            Q81=makeQuery(id+"F3.boolean.opBoolean","INTERSECT",EDGE,{"derivedFrom":[makeQuery(id+"F1.opExtrude","SWEPT_FACE",FACE,{"disambiguationData":[OSD([sQuery(id+"F0.wireOp",EDGE,"E0.top")])]}),makeQuery(id+"F3.opExtrude","SWEPT_FACE",FACE,{"disambiguationData":[OSD([sQuery(id+"F2.wireOp",EDGE,"E36.bottom")])]})]});
            var Q82;
            Q82=makeQuery(id+"F3.boolean.opBoolean","INTERSECT",EDGE,{"derivedFrom":[makeQuery(id+"F1.opExtrude","SWEPT_FACE",FACE,{"disambiguationData":[OSD([sQuery(id+"F0.wireOp",EDGE,"E0.top")])]}),makeQuery(id+"F3.opExtrude","SWEPT_FACE",FACE,{"disambiguationData":[OSD([sQuery(id+"F2.wireOp",EDGE,"E35.bottom")])]})]});
            var Q83;
            Q83=makeQuery(id+"F3.boolean.opBoolean","INTERSECT",EDGE,{"derivedFrom":[makeQuery(id+"F1.opExtrude","SWEPT_FACE",FACE,{"disambiguationData":[OSD([sQuery(id+"F0.wireOp",EDGE,"E0.top")])]}),makeQuery(id+"F3.opExtrude","SWEPT_FACE",FACE,{"disambiguationData":[OSD([sQuery(id+"F2.wireOp",EDGE,"E32.top")])]})]});
            var Q84;
            Q84=makeQuery(id+"F3.boolean.opBoolean","INTERSECT",EDGE,{"derivedFrom":[makeQuery(id+"F1.opExtrude","SWEPT_FACE",FACE,{"disambiguationData":[OSD([sQuery(id+"F0.wireOp",EDGE,"E0.top")])]}),makeQuery(id+"F3.opExtrude","SWEPT_FACE",FACE,{"disambiguationData":[OSD([sQuery(id+"F2.wireOp",EDGE,"E31.top")])]})]});
            var Q85;
            Q85=makeQuery(id+"F3.boolean.opBoolean","INTERSECT",EDGE,{"derivedFrom":[makeQuery(id+"F1.opExtrude","SWEPT_FACE",FACE,{"disambiguationData":[OSD([sQuery(id+"F0.wireOp",EDGE,"E0.top")])]}),makeQuery(id+"F3.opExtrude","SWEPT_FACE",FACE,{"disambiguationData":[OSD([sQuery(id+"F2.wireOp",EDGE,"E34.bottom")])]})]});
            var Q86;
            Q86=makeQuery(id+"F3.boolean.opBoolean","INTERSECT",EDGE,{"derivedFrom":[makeQuery(id+"F1.opExtrude","SWEPT_FACE",FACE,{"disambiguationData":[OSD([sQuery(id+"F0.wireOp",EDGE,"E0.top")])]}),makeQuery(id+"F3.opExtrude","SWEPT_FACE",FACE,{"disambiguationData":[OSD([sQuery(id+"F2.wireOp",EDGE,"E34.right")])]})]});
            var Q87;
            Q87=makeQuery(id+"F3.boolean.opBoolean","INTERSECT",EDGE,{"derivedFrom":[makeQuery(id+"F1.opExtrude","SWEPT_FACE",FACE,{"disambiguationData":[OSD([sQuery(id+"F0.wireOp",EDGE,"E0.top")])]}),makeQuery(id+"F3.opExtrude","SWEPT_FACE",FACE,{"disambiguationData":[OSD([sQuery(id+"F2.wireOp",EDGE,"E35.left")])]})]});
            var Q88;
            Q88=makeQuery(id+"F3.boolean.opBoolean","INTERSECT",EDGE,{"derivedFrom":[makeQuery(id+"F1.opExtrude","SWEPT_FACE",FACE,{"disambiguationData":[OSD([sQuery(id+"F0.wireOp",EDGE,"E0.top")])]}),makeQuery(id+"F3.opExtrude","SWEPT_FACE",FACE,{"disambiguationData":[OSD([sQuery(id+"F2.wireOp",EDGE,"E35.right")])]})]});
            var Q89;
            Q89=makeQuery(id+"F3.boolean.opBoolean","INTERSECT",EDGE,{"derivedFrom":[makeQuery(id+"F1.opExtrude","SWEPT_FACE",FACE,{"disambiguationData":[OSD([sQuery(id+"F0.wireOp",EDGE,"E0.top")])]}),makeQuery(id+"F3.opExtrude","SWEPT_FACE",FACE,{"disambiguationData":[OSD([sQuery(id+"F2.wireOp",EDGE,"E36.left")])]})]});
            var Q90;
            Q90=makeQuery(id+"F3.boolean.opBoolean","INTERSECT",EDGE,{"derivedFrom":[makeQuery(id+"F1.opExtrude","SWEPT_FACE",FACE,{"disambiguationData":[OSD([sQuery(id+"F0.wireOp",EDGE,"E0.top")])]}),makeQuery(id+"F3.opExtrude","SWEPT_FACE",FACE,{"disambiguationData":[OSD([sQuery(id+"F2.wireOp",EDGE,"E36.top")])]})]});
            var Q91;
            Q91=makeQuery(id+"F3.boolean.opBoolean","INTERSECT",EDGE,{"derivedFrom":[makeQuery(id+"F1.opExtrude","SWEPT_FACE",FACE,{"disambiguationData":[OSD([sQuery(id+"F0.wireOp",EDGE,"E0.top")])]}),makeQuery(id+"F3.opExtrude","SWEPT_FACE",FACE,{"disambiguationData":[OSD([sQuery(id+"F2.wireOp",EDGE,"E39.bottom")])]})]});
            var Q92;
            Q92=makeQuery(id+"F3.boolean.opBoolean","INTERSECT",EDGE,{"derivedFrom":[makeQuery(id+"F1.opExtrude","SWEPT_FACE",FACE,{"disambiguationData":[OSD([sQuery(id+"F0.wireOp",EDGE,"E0.top")])]}),makeQuery(id+"F3.opExtrude","SWEPT_FACE",FACE,{"disambiguationData":[OSD([sQuery(id+"F2.wireOp",EDGE,"E38.bottom")])]})]});
            var Q93;
            Q93=makeQuery(id+"F3.boolean.opBoolean","INTERSECT",EDGE,{"derivedFrom":[makeQuery(id+"F1.opExtrude","SWEPT_FACE",FACE,{"disambiguationData":[OSD([sQuery(id+"F0.wireOp",EDGE,"E0.top")])]}),makeQuery(id+"F3.opExtrude","SWEPT_FACE",FACE,{"disambiguationData":[OSD([sQuery(id+"F2.wireOp",EDGE,"E35.top")])]})]});
            var Q94;
            Q94=makeQuery(id+"F3.boolean.opBoolean","INTERSECT",EDGE,{"derivedFrom":[makeQuery(id+"F1.opExtrude","SWEPT_FACE",FACE,{"disambiguationData":[OSD([sQuery(id+"F0.wireOp",EDGE,"E0.top")])]}),makeQuery(id+"F3.opExtrude","SWEPT_FACE",FACE,{"disambiguationData":[OSD([sQuery(id+"F2.wireOp",EDGE,"E34.top")])]})]});
            var Q95;
            Q95=makeQuery(id+"F3.boolean.opBoolean","INTERSECT",EDGE,{"derivedFrom":[makeQuery(id+"F1.opExtrude","SWEPT_FACE",FACE,{"disambiguationData":[OSD([sQuery(id+"F0.wireOp",EDGE,"E0.top")])]}),makeQuery(id+"F3.opExtrude","SWEPT_FACE",FACE,{"disambiguationData":[OSD([sQuery(id+"F2.wireOp",EDGE,"E37.bottom")])]})]});
            var Q96;
            Q96=makeQuery(id+"F3.boolean.opBoolean","INTERSECT",EDGE,{"derivedFrom":[makeQuery(id+"F1.opExtrude","SWEPT_FACE",FACE,{"disambiguationData":[OSD([sQuery(id+"F0.wireOp",EDGE,"E0.top")])]}),makeQuery(id+"F3.opExtrude","SWEPT_FACE",FACE,{"disambiguationData":[OSD([sQuery(id+"F2.wireOp",EDGE,"E37.right")])]})]});
            var Q97;
            Q97=makeQuery(id+"F3.boolean.opBoolean","INTERSECT",EDGE,{"derivedFrom":[makeQuery(id+"F1.opExtrude","SWEPT_FACE",FACE,{"disambiguationData":[OSD([sQuery(id+"F0.wireOp",EDGE,"E0.top")])]}),makeQuery(id+"F3.opExtrude","SWEPT_FACE",FACE,{"disambiguationData":[OSD([sQuery(id+"F2.wireOp",EDGE,"E38.left")])]})]});
            var Q98;
            Q98=makeQuery(id+"F3.boolean.opBoolean","INTERSECT",EDGE,{"derivedFrom":[makeQuery(id+"F1.opExtrude","SWEPT_FACE",FACE,{"disambiguationData":[OSD([sQuery(id+"F0.wireOp",EDGE,"E0.top")])]}),makeQuery(id+"F3.opExtrude","SWEPT_FACE",FACE,{"disambiguationData":[OSD([sQuery(id+"F2.wireOp",EDGE,"E38.right")])]})]});
            var Q99;
            Q99=makeQuery(id+"F3.boolean.opBoolean","INTERSECT",EDGE,{"derivedFrom":[makeQuery(id+"F1.opExtrude","SWEPT_FACE",FACE,{"disambiguationData":[OSD([sQuery(id+"F0.wireOp",EDGE,"E0.top")])]}),makeQuery(id+"F3.opExtrude","SWEPT_FACE",FACE,{"disambiguationData":[OSD([sQuery(id+"F2.wireOp",EDGE,"E39.left")])]})]});
            var Q100;
            Q100=makeQuery(id+"F3.boolean.opBoolean","INTERSECT",EDGE,{"derivedFrom":[makeQuery(id+"F1.opExtrude","SWEPT_FACE",FACE,{"disambiguationData":[OSD([sQuery(id+"F0.wireOp",EDGE,"E0.top")])]}),makeQuery(id+"F3.opExtrude","SWEPT_FACE",FACE,{"disambiguationData":[OSD([sQuery(id+"F2.wireOp",EDGE,"E37.top")])]})]});
            var Q101;
            Q101=makeQuery(id+"F3.boolean.opBoolean","INTERSECT",EDGE,{"derivedFrom":[makeQuery(id+"F1.opExtrude","SWEPT_FACE",FACE,{"disambiguationData":[OSD([sQuery(id+"F0.wireOp",EDGE,"E0.top")])]}),makeQuery(id+"F3.opExtrude","SWEPT_FACE",FACE,{"disambiguationData":[OSD([sQuery(id+"F2.wireOp",EDGE,"E38.top")])]})]});
            var Q102;
            Q102=makeQuery(id+"F3.boolean.opBoolean","INTERSECT",EDGE,{"derivedFrom":[makeQuery(id+"F1.opExtrude","SWEPT_FACE",FACE,{"disambiguationData":[OSD([sQuery(id+"F0.wireOp",EDGE,"E0.top")])]}),makeQuery(id+"F3.opExtrude","SWEPT_FACE",FACE,{"disambiguationData":[OSD([sQuery(id+"F2.wireOp",EDGE,"E39.top")])]})]});
            var Q103;
            Q103=makeQuery(id+"F3.boolean.opBoolean","INTERSECT",EDGE,{"derivedFrom":[makeQuery(id+"F1.opExtrude","SWEPT_FACE",FACE,{"disambiguationData":[OSD([sQuery(id+"F0.wireOp",EDGE,"E0.top")])]}),makeQuery(id+"F3.opExtrude","SWEPT_FACE",FACE,{"disambiguationData":[OSD([sQuery(id+"F2.wireOp",EDGE,"E42.bottom")])]})]});
            var Q104;
            Q104=makeQuery(id+"F3.boolean.opBoolean","INTERSECT",EDGE,{"derivedFrom":[makeQuery(id+"F1.opExtrude","SWEPT_FACE",FACE,{"disambiguationData":[OSD([sQuery(id+"F0.wireOp",EDGE,"E0.top")])]}),makeQuery(id+"F3.opExtrude","SWEPT_FACE",FACE,{"disambiguationData":[OSD([sQuery(id+"F2.wireOp",EDGE,"E41.bottom")])]})]});
            var Q105;
            Q105=makeQuery(id+"F3.boolean.opBoolean","INTERSECT",EDGE,{"derivedFrom":[makeQuery(id+"F1.opExtrude","SWEPT_FACE",FACE,{"disambiguationData":[OSD([sQuery(id+"F0.wireOp",EDGE,"E0.top")])]}),makeQuery(id+"F3.opExtrude","SWEPT_FACE",FACE,{"disambiguationData":[OSD([sQuery(id+"F2.wireOp",EDGE,"E40.bottom")])]})]});
            var Q106;
            Q106=makeQuery(id+"F3.boolean.opBoolean","INTERSECT",EDGE,{"derivedFrom":[makeQuery(id+"F1.opExtrude","SWEPT_FACE",FACE,{"disambiguationData":[OSD([sQuery(id+"F0.wireOp",EDGE,"E0.top")])]}),makeQuery(id+"F3.opExtrude","SWEPT_FACE",FACE,{"disambiguationData":[OSD([sQuery(id+"F2.wireOp",EDGE,"E40.right")])]})]});
            var Q107;
            Q107=makeQuery(id+"F3.boolean.opBoolean","INTERSECT",EDGE,{"derivedFrom":[makeQuery(id+"F1.opExtrude","SWEPT_FACE",FACE,{"disambiguationData":[OSD([sQuery(id+"F0.wireOp",EDGE,"E0.top")])]}),makeQuery(id+"F3.opExtrude","SWEPT_FACE",FACE,{"disambiguationData":[OSD([sQuery(id+"F2.wireOp",EDGE,"E41.left")])]})]});
            var Q108;
            Q108=makeQuery(id+"F3.boolean.opBoolean","INTERSECT",EDGE,{"derivedFrom":[makeQuery(id+"F1.opExtrude","SWEPT_FACE",FACE,{"disambiguationData":[OSD([sQuery(id+"F0.wireOp",EDGE,"E0.top")])]}),makeQuery(id+"F3.opExtrude","SWEPT_FACE",FACE,{"disambiguationData":[OSD([sQuery(id+"F2.wireOp",EDGE,"E41.right")])]})]});
            var Q109;
            Q109=makeQuery(id+"F3.boolean.opBoolean","INTERSECT",EDGE,{"derivedFrom":[makeQuery(id+"F1.opExtrude","SWEPT_FACE",FACE,{"disambiguationData":[OSD([sQuery(id+"F0.wireOp",EDGE,"E0.top")])]}),makeQuery(id+"F3.opExtrude","SWEPT_FACE",FACE,{"disambiguationData":[OSD([sQuery(id+"F2.wireOp",EDGE,"E42.left")])]})]});
            var Q110;
            Q110=makeQuery(id+"F3.boolean.opBoolean","INTERSECT",EDGE,{"derivedFrom":[makeQuery(id+"F1.opExtrude","SWEPT_FACE",FACE,{"disambiguationData":[OSD([sQuery(id+"F0.wireOp",EDGE,"E0.top")])]}),makeQuery(id+"F3.opExtrude","SWEPT_FACE",FACE,{"disambiguationData":[OSD([sQuery(id+"F2.wireOp",EDGE,"E42.top")])]})]});
            var Q111;
            Q111=makeQuery(id+"F3.boolean.opBoolean","INTERSECT",EDGE,{"derivedFrom":[makeQuery(id+"F1.opExtrude","SWEPT_FACE",FACE,{"disambiguationData":[OSD([sQuery(id+"F0.wireOp",EDGE,"E0.top")])]}),makeQuery(id+"F3.opExtrude","SWEPT_FACE",FACE,{"disambiguationData":[OSD([sQuery(id+"F2.wireOp",EDGE,"E45.bottom")])]})]});
            var Q112;
            Q112=makeQuery(id+"F3.boolean.opBoolean","INTERSECT",EDGE,{"derivedFrom":[makeQuery(id+"F1.opExtrude","SWEPT_FACE",FACE,{"disambiguationData":[OSD([sQuery(id+"F0.wireOp",EDGE,"E0.top")])]}),makeQuery(id+"F3.opExtrude","SWEPT_FACE",FACE,{"disambiguationData":[OSD([sQuery(id+"F2.wireOp",EDGE,"E44.bottom")])]})]});
            var Q113;
            Q113=makeQuery(id+"F3.boolean.opBoolean","INTERSECT",EDGE,{"derivedFrom":[makeQuery(id+"F1.opExtrude","SWEPT_FACE",FACE,{"disambiguationData":[OSD([sQuery(id+"F0.wireOp",EDGE,"E0.top")])]}),makeQuery(id+"F3.opExtrude","SWEPT_FACE",FACE,{"disambiguationData":[OSD([sQuery(id+"F2.wireOp",EDGE,"E41.top")])]})]});
            var Q114;
            Q114=makeQuery(id+"F3.boolean.opBoolean","INTERSECT",EDGE,{"derivedFrom":[makeQuery(id+"F1.opExtrude","SWEPT_FACE",FACE,{"disambiguationData":[OSD([sQuery(id+"F0.wireOp",EDGE,"E0.top")])]}),makeQuery(id+"F3.opExtrude","SWEPT_FACE",FACE,{"disambiguationData":[OSD([sQuery(id+"F2.wireOp",EDGE,"E43.bottom")])]})]});
            var Q115;
            Q115=makeQuery(id+"F3.boolean.opBoolean","INTERSECT",EDGE,{"derivedFrom":[makeQuery(id+"F1.opExtrude","SWEPT_FACE",FACE,{"disambiguationData":[OSD([sQuery(id+"F0.wireOp",EDGE,"E0.top")])]}),makeQuery(id+"F3.opExtrude","SWEPT_FACE",FACE,{"disambiguationData":[OSD([sQuery(id+"F2.wireOp",EDGE,"E40.top")])]})]});
            var Q116;
            Q116=makeQuery(id+"F3.boolean.opBoolean","INTERSECT",EDGE,{"derivedFrom":[makeQuery(id+"F1.opExtrude","SWEPT_FACE",FACE,{"disambiguationData":[OSD([sQuery(id+"F0.wireOp",EDGE,"E0.top")])]}),makeQuery(id+"F3.opExtrude","SWEPT_FACE",FACE,{"disambiguationData":[OSD([sQuery(id+"F2.wireOp",EDGE,"E43.right")])]})]});
            var Q117;
            Q117=makeQuery(id+"F3.boolean.opBoolean","INTERSECT",EDGE,{"derivedFrom":[makeQuery(id+"F1.opExtrude","SWEPT_FACE",FACE,{"disambiguationData":[OSD([sQuery(id+"F0.wireOp",EDGE,"E0.top")])]}),makeQuery(id+"F3.opExtrude","SWEPT_FACE",FACE,{"disambiguationData":[OSD([sQuery(id+"F2.wireOp",EDGE,"E44.left")])]})]});
            var Q118;
            Q118=makeQuery(id+"F3.boolean.opBoolean","INTERSECT",EDGE,{"derivedFrom":[makeQuery(id+"F1.opExtrude","SWEPT_FACE",FACE,{"disambiguationData":[OSD([sQuery(id+"F0.wireOp",EDGE,"E0.top")])]}),makeQuery(id+"F3.opExtrude","SWEPT_FACE",FACE,{"disambiguationData":[OSD([sQuery(id+"F2.wireOp",EDGE,"E44.right")])]})]});
            var Q119;
            Q119=makeQuery(id+"F3.boolean.opBoolean","INTERSECT",EDGE,{"derivedFrom":[makeQuery(id+"F1.opExtrude","SWEPT_FACE",FACE,{"disambiguationData":[OSD([sQuery(id+"F0.wireOp",EDGE,"E0.top")])]}),makeQuery(id+"F3.opExtrude","SWEPT_FACE",FACE,{"disambiguationData":[OSD([sQuery(id+"F2.wireOp",EDGE,"E45.left")])]})]});
            chamfer(context, id + "F4", {"entities" : qUnion([Q0, Q1, Q2, Q3, Q4, Q5, Q6, Q7, Q8, Q9, Q10, Q11, Q12, Q13, Q14, Q15, Q16, Q17, Q18, Q19, Q20, Q21, Q22, Q23, Q24, Q25, Q26, Q27, Q28, Q29, Q30, Q31, Q32, Q33, Q34, Q35, Q36, Q37, Q38, Q39, Q40, Q41, Q42, Q43, Q44, Q45, Q46, Q47, Q48, Q49, Q50, Q51, Q52, Q53, Q54, Q55, Q56, Q57, Q58, Q59, Q60, Q61, Q62, Q63, Q64, Q65, Q66, Q67, Q68, Q69, Q70, Q71, Q72, Q73, Q74, Q75, Q76, Q77, Q78, Q79, Q80, Q81, Q82, Q83, Q84, Q85, Q86, Q87, Q88, Q89, Q90, Q91, Q92, Q93, Q94, Q95, Q96, Q97, Q98, Q99, Q100, Q101, Q102, Q103, Q104, Q105, Q106, Q107, Q108, Q109, Q110, Q111, Q112, Q113, Q114, Q115, Q116, Q117, Q118, Q119]), "width" : 7.94 * mm, "tangentPropagation" : true});
        }
    });
